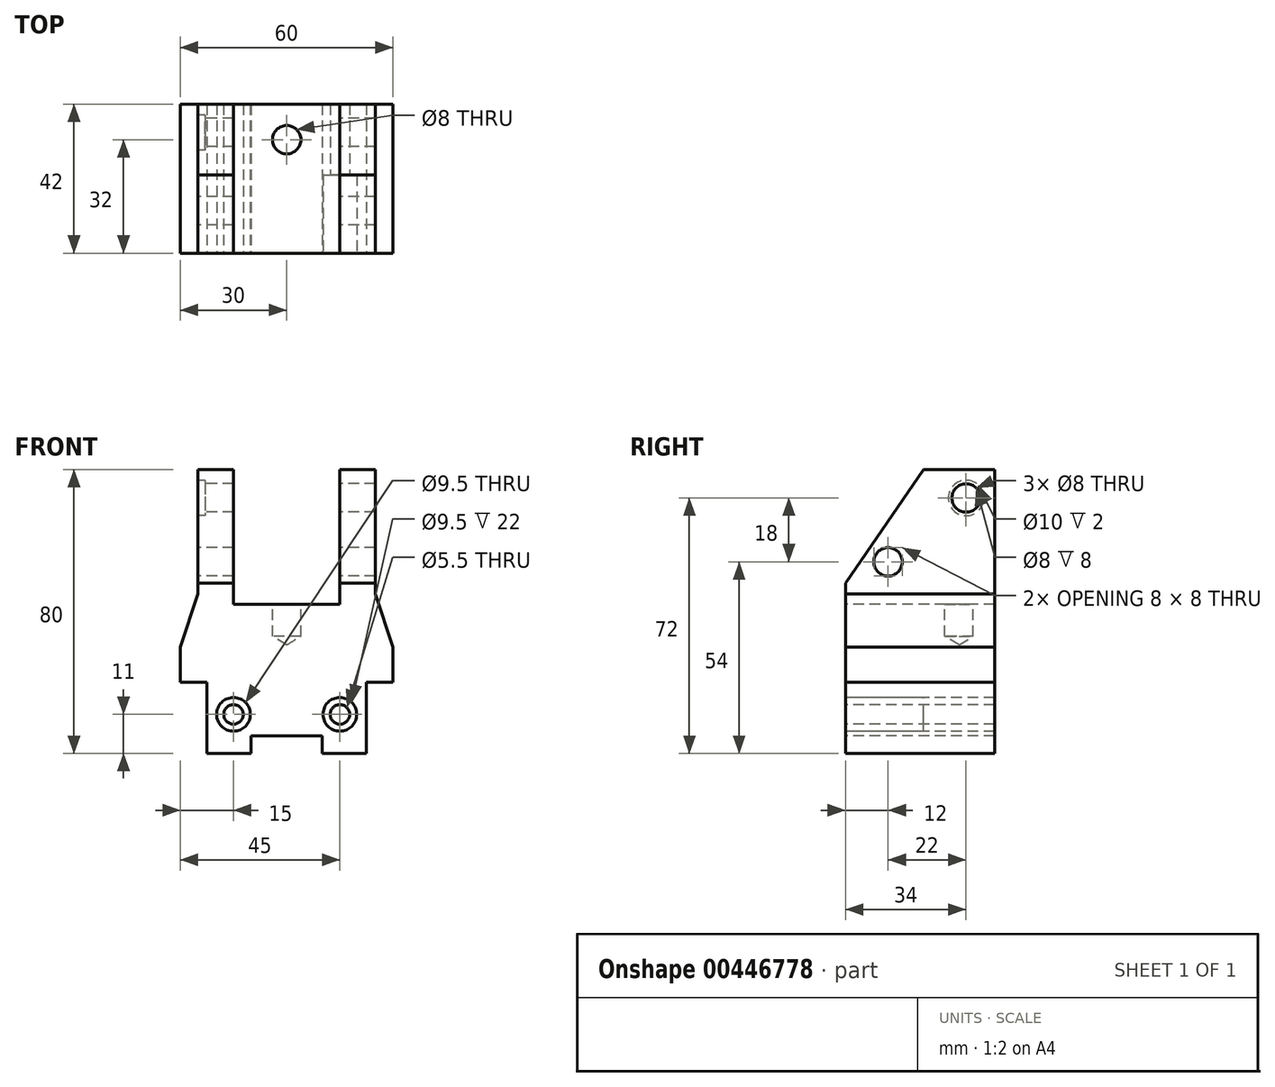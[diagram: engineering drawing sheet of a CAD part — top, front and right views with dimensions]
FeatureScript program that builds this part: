
annotation { "Feature Type Name" : "Feature", "Feature Type Description" : "" }
export const myFeature = defineFeature(function(context is Context, id is Id, definition is map)
    precondition{}
    {
        {
            var Q0;
            Q0=qCreatedBy(makeId("Right.planeOp"),FACE);
            var sketch = newSketch(context, id + "F0", { "sketchPlane" : qUnion([Q0])});
            skLineSegment(sketch, "E0.bottom", {"start": v(21, 40) * mm, "end": v(1, 40) * mm});
            skLineSegment(sketch, "E0.top", {"start": v(21, -40) * mm, "end": v(-21, -40) * mm});
            skLineSegment(sketch, "E0.left", {"start": v(21, 40) * mm, "end": v(21, -40) * mm});
            skLineSegment(sketch, "E0.right", {"start": v(-21, 8) * mm, "end": v(-21, -40) * mm});
            skPoint(sketch, "E0.middle", {"position": v(0, 0) * mm});
            skLineSegment(sketch, "E1", {"start": v(-21, 8) * mm, "end": v(1, 40) * mm});
            skPoint(sketch, "E2.orphan", {"position": v(-21, 40) * mm});
            skSolve(sketch);
        }
        {
            var Q0;
            Q0 = qSketchRegion(id + "F0", true);
            extrude(context, id + "F1", {"entities" : qUnion([Q0]), "depth" : 60 * mm, "symmetric" : true});
        }
        {
            var Q0;
            Q0=makeQuery(id+"F1.opExtrude","SWEPT_FACE",FACE,{"disambiguationData":[OSD([sQuery(id+"F0.wireOp",EDGE,"E0.right")])]});
            var sketch = newSketch(context, id + "F2", { "sketchPlane" : qUnion([Q0])});
            skLineSegment(sketch, "E3.0", {"start": v(30, 40) * mm, "end": v(25, 40) * mm});
            skLineSegment(sketch, "E4.bottom", {"start": v(-15, 2) * mm, "end": v(15, 2) * mm});
            skLineSegment(sketch, "E4.top", {"start": v(-15, 40) * mm, "end": v(15, 40) * mm});
            skLineSegment(sketch, "E4.left", {"start": v(-15, 2) * mm, "end": v(-15, 40) * mm});
            skLineSegment(sketch, "E4.right", {"start": v(15, 2) * mm, "end": v(15, 40) * mm});
            skLineSegment(sketch, "E5.bottom", {"start": v(-30, -20) * mm, "end": v(-22.5, -20) * mm});
            skLineSegment(sketch, "E5.top", {"start": v(-30, -40) * mm, "end": v(-22.5, -40) * mm});
            skLineSegment(sketch, "E5.left", {"start": v(-30, -20) * mm, "end": v(-30, -40) * mm});
            skLineSegment(sketch, "E5.right", {"start": v(-22.5, -20) * mm, "end": v(-22.5, -40) * mm});
            skLineSegment(sketch, "E6", {"start": v(0, 0) * mm, "end": v(0, -17.86) * mm, "construction": true});
            skLineSegment(sketch, "E7.MirrorCS", {"start": v(30, -20) * mm, "end": v(22.5, -20) * mm});
            skLineSegment(sketch, "E8.MirrorCS", {"start": v(30, -20) * mm, "end": v(30, -40) * mm});
            skLineSegment(sketch, "E9.MirrorCS", {"start": v(22.5, -20) * mm, "end": v(22.5, -40) * mm});
            skLineSegment(sketch, "E10.MirrorCS", {"start": v(30, -40) * mm, "end": v(22.5, -40) * mm});
            skLineSegment(sketch, "E11", {"start": v(30, -10) * mm, "end": v(25, 5) * mm});
            skLineSegment(sketch, "E12", {"start": v(25, 5) * mm, "end": v(25, 40) * mm});
            skLineSegment(sketch, "E13.MirrorCS", {"start": v(-25, 5) * mm, "end": v(-25, 40) * mm});
            skLineSegment(sketch, "E14.MirrorCS", {"start": v(-30, -10) * mm, "end": v(-25, 5) * mm});
            skLineSegment(sketch, "E15.0", {"start": v(-30, 8) * mm, "end": v(-30, 40) * mm});
            skLineSegment(sketch, "E16.0", {"start": v(-30, 8) * mm, "end": v(-30, -10) * mm});
            skLineSegment(sketch, "E17.0", {"start": v(30, 8) * mm, "end": v(30, 40) * mm});
            skLineSegment(sketch, "E18.0", {"start": v(30, 8) * mm, "end": v(30, -10) * mm});
            skLineSegment(sketch, "E19.trimOffspring", {"start": v(-25, 40) * mm, "end": v(-30, 40) * mm});
            skLineSegment(sketch, "E20.trimOffspring", {"start": v(15, 40) * mm, "end": v(-15, 40) * mm});
            skLineSegment(sketch, "E21.bottom", {"start": v(-10, -40) * mm, "end": v(10, -40) * mm});
            skLineSegment(sketch, "E21.top", {"start": v(-10, -35) * mm, "end": v(10, -35) * mm});
            skLineSegment(sketch, "E21.left", {"start": v(-10, -40) * mm, "end": v(-10, -35) * mm});
            skLineSegment(sketch, "E21.right", {"start": v(10, -40) * mm, "end": v(10, -35) * mm});
            skSolve(sketch);
        }
        {
            var Q0;
            Q0 = qSketchRegion(id + "F2", true);
            extrude(context, id + "F3", {"entities" : qUnion([Q0]), "operationType" : NewBodyOperationType.REMOVE, "oppositeDirection" : true, "depth" : 42 * mm});
        }
        {
            var Q0;
            Q0=makeQuery(id+"F1.opExtrude","SWEPT_FACE",FACE,{"disambiguationData":[OSD([sQuery(id+"F0.wireOp",EDGE,"E0.right")])]});
            var sketch = newSketch(context, id + "F4", { "sketchPlane" : qUnion([Q0])});
            skLineSegment(sketch, "E22", {"start": v(0, 0) * mm, "end": v(0, -9.02) * mm, "construction": true});
            skCircle(sketch, "E23", {"center": v(15, -29) * mm, "radius": 4.75 * mm});
            skCircle(sketch, "E24", {"center": v(15, -29) * mm, "radius": 2.75 * mm});
            skCircle(sketch, "E25.MirrorC", {"center": v(-15, -29) * mm, "radius": 4.75 * mm});
            skCircle(sketch, "E26.MirrorC", {"center": v(-15, -29) * mm, "radius": 2.75 * mm});
            skSolve(sketch);
        }
        {
            var Q0;
            Q0 = qSketchRegion(id + "F4", true);
            var Q1;
            Q1=makeQuery(id+"F4.imprint","IMPRINT",FACE,{"disambiguationData":[TD([[makeQuery(id+"F4.imprint","IMPRINT",EDGE,{"derivedFrom":sQuery(id+"F4.wireOp",EDGE,"E26.MirrorC")}),-1.0]])]});
            var Q2;
            Q2=makeQuery(id+"F4.imprint","IMPRINT",FACE,{"disambiguationData":[TD([[makeQuery(id+"F4.imprint","IMPRINT",EDGE,{"derivedFrom":sQuery(id+"F4.wireOp",EDGE,"E24")}),1.0]])]});
            extrude(context, id + "F5", {"entities" : qUnion([Q0, Q1, Q2]), "operationType" : NewBodyOperationType.REMOVE, "oppositeDirection" : true, "depth" : 22 * mm});
        }
        {
            var Q0;
            Q0=makeQuery(id+"F4.imprint","IMPRINT",FACE,{"disambiguationData":[TD([[makeQuery(id+"F4.imprint","IMPRINT",EDGE,{"derivedFrom":sQuery(id+"F4.wireOp",EDGE,"E26.MirrorC")}),-1.0]])]});
            var Q1;
            Q1=makeQuery(id+"F4.imprint","IMPRINT",FACE,{"disambiguationData":[TD([[makeQuery(id+"F4.imprint","IMPRINT",EDGE,{"derivedFrom":sQuery(id+"F4.wireOp",EDGE,"E24")}),1.0]])]});
            extrude(context, id + "F6", {"entities" : qUnion([Q0, Q1]), "operationType" : NewBodyOperationType.REMOVE, "oppositeDirection" : true, "depth" : 42 * mm});
        }
        {
            var Q0;
            Q0=makeQuery(id+"F3.boolean.opBoolean","COPY",FACE,{"derivedFrom":makeQuery(id+"F3.opExtrude","SWEPT_FACE",FACE,{"disambiguationData":[OSD([sQuery(id+"F2.wireOp",EDGE,"E4.bottom")])]})});
            var sketch = newSketch(context, id + "F7", { "sketchPlane" : qUnion([Q0])});
            skPoint(sketch, "E27", {"position": v(0, 11) * mm});
            skSolve(sketch);
        }
        {
            var Q0;
            Q0=sQuery(id+"F7.wireOp",VERTEX,"E27");
            var Q1;
            Q1=makeQuery(id+"F1.opExtrude","SWEPT_BODY",BODY,{"disambiguationData":[OSD([sQuery(id+"F0.wireOp",EDGE,"E0.bottom"),sQuery(id+"F0.wireOp",EDGE,"E0.top"),sQuery(id+"F0.wireOp",EDGE,"E0.left"),sQuery(id+"F0.wireOp",EDGE,"E0.right"),sQuery(id+"F0.wireOp",EDGE,"E1")])]});
            hole(context, id + "F8", {"style" : HoleStyle.SIMPLE, "endStyle" : HoleEndStyle.BLIND, "holeDiameter" : 8 * mm, "holeDepth" : 9 * mm, "isTappedThrough" : true, "tappedDepth" : 12 * mm, "tapClearance" : 3, "startFromSketch" : true, "locations" : qUnion([Q0]), "scope" : qUnion([Q1])});
        }
        {
            var Q0;
            Q0=makeQuery(id+"F3.boolean.opBoolean","COPY",FACE,{"derivedFrom":makeQuery(id+"F3.opExtrude","SWEPT_FACE",FACE,{"disambiguationData":[OSD([sQuery(id+"F2.wireOp",EDGE,"E13.MirrorCS")])]})});
            var sketch = newSketch(context, id + "F9", { "sketchPlane" : qUnion([Q0])});
            skPoint(sketch, "E28", {"position": v(-13, 32) * mm});
            skPoint(sketch, "E29", {"position": v(9, 14) * mm});
            skSolve(sketch);
        }
        {
            var Q0;
            Q0=sQuery(id+"F9.wireOp",VERTEX,"E28");
            var Q1;
            Q1=makeQuery(id+"F1.opExtrude","SWEPT_BODY",BODY,{"disambiguationData":[OSD([sQuery(id+"F0.wireOp",EDGE,"E0.bottom"),sQuery(id+"F0.wireOp",EDGE,"E0.top"),sQuery(id+"F0.wireOp",EDGE,"E0.left"),sQuery(id+"F0.wireOp",EDGE,"E0.right"),sQuery(id+"F0.wireOp",EDGE,"E1")])]});
            hole(context, id + "F10", {"style" : HoleStyle.C_BORE, "endStyle" : HoleEndStyle.BLIND, "holeDiameter" : 8 * mm, "cBoreDiameter" : 10 * mm, "cBoreDepth" : 2 * mm, "holeDepth" : 50 * mm, "isTappedThrough" : true, "tappedDepth" : 12 * mm, "tapClearance" : 3, "startFromSketch" : true, "locations" : qUnion([Q0]), "scope" : qUnion([Q1])});
        }
        {
            var Q0;
            Q0=sQuery(id+"F9.wireOp",VERTEX,"E29");
            var Q1;
            Q1=makeQuery(id+"F1.opExtrude","SWEPT_BODY",BODY,{"disambiguationData":[OSD([sQuery(id+"F0.wireOp",EDGE,"E0.bottom"),sQuery(id+"F0.wireOp",EDGE,"E0.top"),sQuery(id+"F0.wireOp",EDGE,"E0.left"),sQuery(id+"F0.wireOp",EDGE,"E0.right"),sQuery(id+"F0.wireOp",EDGE,"E1")])]});
            hole(context, id + "F11", {"style" : HoleStyle.SIMPLE, "endStyle" : HoleEndStyle.BLIND, "holeDiameter" : 8 * mm, "holeDepth" : 50 * mm, "isTappedThrough" : true, "tappedDepth" : 12 * mm, "tapClearance" : 3, "startFromSketch" : true, "locations" : qUnion([Q0]), "scope" : qUnion([Q1])});
        }
    });
